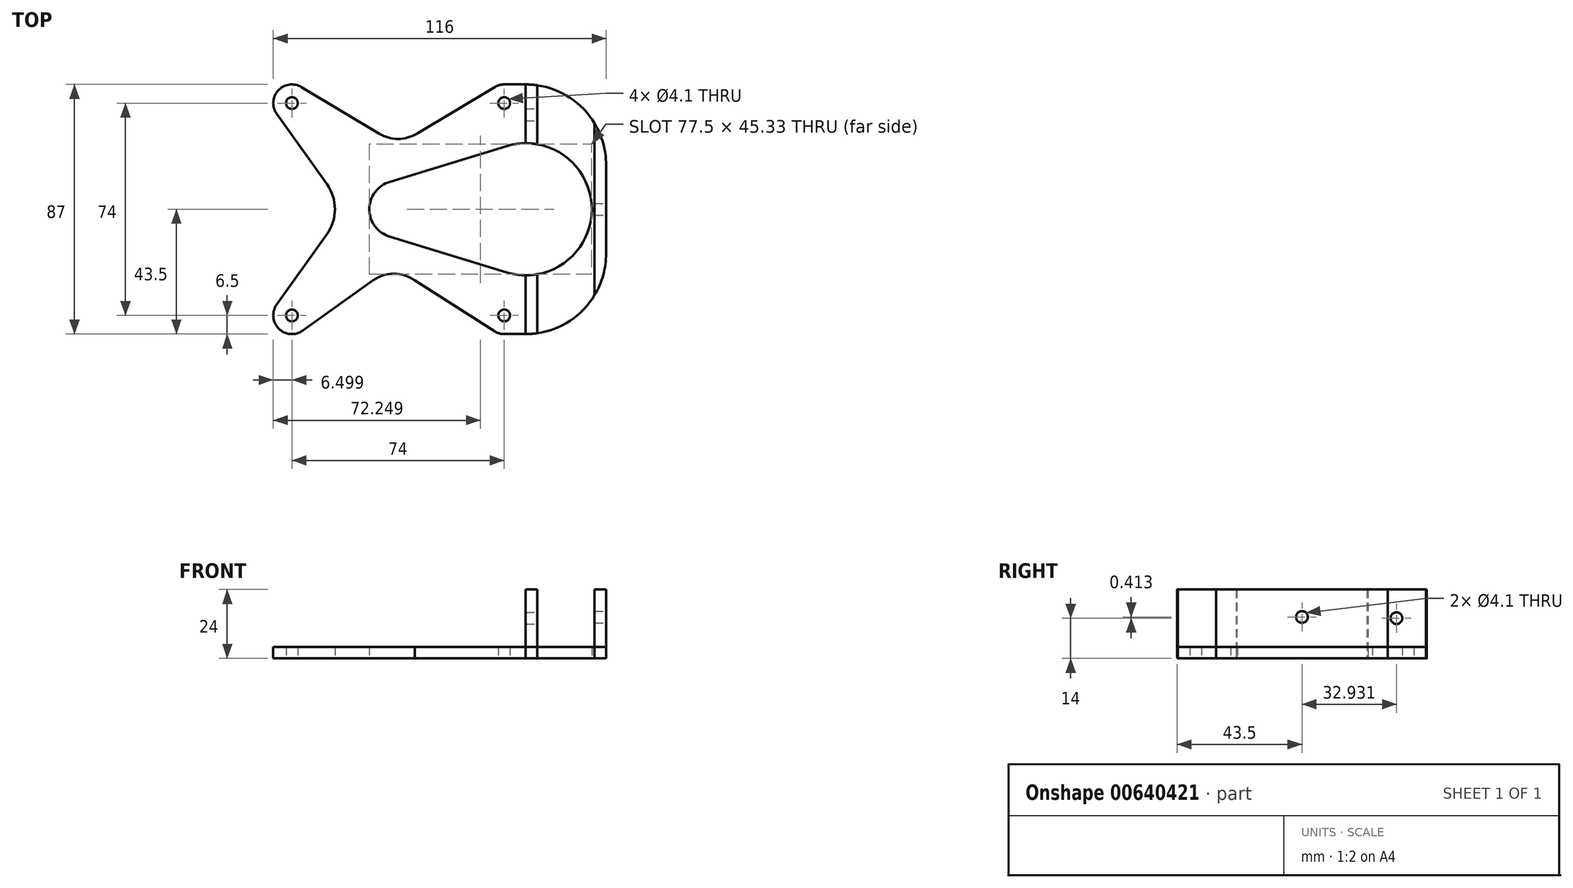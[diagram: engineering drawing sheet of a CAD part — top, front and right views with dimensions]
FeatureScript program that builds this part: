
annotation { "Feature Type Name" : "Feature", "Feature Type Description" : "" }
export const myFeature = defineFeature(function(context is Context, id is Id, definition is map)
    precondition{}
    {
        {
            var Q0;
            Q0=qCreatedBy(makeId("Top.planeOp"),FACE);
            var sketch = newSketch(context, id + "F0", { "sketchPlane" : qUnion([Q0])});
            skLineSegment(sketch, "E0.bottom", {"start": v(-43.02, 41.5) * mm, "end": v(95.48, 41.5) * mm});
            skLineSegment(sketch, "E0.top", {"start": v(-43.02, -41.5) * mm, "end": v(95.48, -41.5) * mm});
            skLineSegment(sketch, "E0.left", {"start": v(-43.02, 41.5) * mm, "end": v(-43.02, -41.5) * mm});
            skLineSegment(sketch, "E0.right", {"start": v(95.48, 41.5) * mm, "end": v(95.48, -41.5) * mm});
            skLineSegment(sketch, "E1", {"start": v(-34.02, 60.46) * mm, "end": v(-34.02, -47.61) * mm, "construction": true});
            skLineSegment(sketch, "E2", {"start": v(-53.58, 0) * mm, "end": v(72.53, 0) * mm, "construction": true});
            skLineSegment(sketch, "E3", {"start": v(-46.55, 37) * mm, "end": v(71.96, 37) * mm, "construction": true});
            skLineSegment(sketch, "E4", {"start": v(-45.6, -37) * mm, "end": v(74.43, -37) * mm, "construction": true});
            skLineSegment(sketch, "E5", {"start": v(39.98, 59.32) * mm, "end": v(39.98, -47.8) * mm, "construction": true});
            skCircle(sketch, "E6", {"center": v(-34.02, 37) * mm, "radius": 2.05 * mm});
            skCircle(sketch, "E7", {"center": v(-34.02, -37) * mm, "radius": 2.05 * mm});
            skCircle(sketch, "E8", {"center": v(39.98, 37) * mm, "radius": 2.05 * mm});
            skCircle(sketch, "E9", {"center": v(39.98, -37) * mm, "radius": 2.05 * mm});
            skLineSegment(sketch, "E10", {"start": v(47.48, 53.05) * mm, "end": v(47.48, -49.7) * mm, "construction": true});
            skLineSegment(sketch, "E11", {"start": v(71.48, 54) * mm, "end": v(71.48, 41.5) * mm, "construction": true});
            skLineSegment(sketch, "E12", {"start": v(51.48, 53.2) * mm, "end": v(51.48, -45.93) * mm, "construction": true});
            skLineSegment(sketch, "E13", {"start": v(75.48, 54.1) * mm, "end": v(75.48, 41.5) * mm, "construction": true});
            skArc(sketch, "E14", {"start": v(-30.68, 42.58) * mm, "mid": v(-38.8, 41.4) * mm, "end": v(-39.31, 33.22) * mm});
            skArc(sketch, "E15", {"start": v(-39.31, -33.22) * mm, "mid": v(-38.62, -41.6) * mm, "end": v(-30.24, -42.29) * mm});
            skArc(sketch, "E16", {"start": v(36.48, -42.48) * mm, "mid": v(38.16, -43.24) * mm, "end": v(39.98, -43.5) * mm});
            skLineSegment(sketch, "E17", {"start": v(2.98, 52.33) * mm, "end": v(2.98, -45.98) * mm, "construction": true});
            skArc(sketch, "E18", {"start": v(-3.44, 26.27) * mm, "mid": v(2.98, 24.5) * mm, "end": v(9.4, 26.27) * mm});
            skArc(sketch, "E19", {"start": v(40.76, -22) * mm, "mid": v(70.48, 0) * mm, "end": v(40.76, 22) * mm});
            skArc(sketch, "E20", {"start": v(0.06, 9.56) * mm, "mid": v(-7.02, 0) * mm, "end": v(0.06, -9.56) * mm});
            skLineSegment(sketch, "E21", {"start": v(-39.31, 33.22) * mm, "end": v(-21.81, 8.72) * mm});
            skLineSegment(sketch, "E22", {"start": v(-30.68, 42.58) * mm, "end": v(-3.44, 26.27) * mm});
            skLineSegment(sketch, "E23", {"start": v(-21.81, -8.72) * mm, "end": v(-39.31, -33.22) * mm});
            skLineSegment(sketch, "E24", {"start": v(-30.24, -42.29) * mm, "end": v(-5.74, -24.8) * mm});
            skLineSegment(sketch, "E25", {"start": v(36.48, -42.48) * mm, "end": v(8.79, -24.8) * mm});
            skLineSegment(sketch, "E26", {"start": v(0.06, 9.56) * mm, "end": v(40.76, 22) * mm});
            skLineSegment(sketch, "E27", {"start": v(0.06, -9.56) * mm, "end": v(40.76, -22) * mm});
            skLineSegment(sketch, "E28", {"start": v(39.98, 43.5) * mm, "end": v(47.48, 43.5) * mm});
            skLineSegment(sketch, "E29", {"start": v(39.98, -43.5) * mm, "end": v(47.48, -43.5) * mm});
            skLineSegment(sketch, "E30", {"start": v(75.48, 43.5) * mm, "end": v(75.48, -43.5) * mm});
            skArc(sketch, "E31.trimOffspring", {"start": v(-21.81, -8.72) * mm, "mid": v(-19.02, 0) * mm, "end": v(-21.81, 8.72) * mm});
            skArc(sketch, "E32.trimOffspring", {"start": v(8.79, -24.8) * mm, "mid": v(1.53, -22.47) * mm, "end": v(-5.74, -24.8) * mm});
            skLineSegment(sketch, "E33", {"start": v(47.48, 43.5) * mm, "end": v(47.48, 23) * mm});
            skLineSegment(sketch, "E34", {"start": v(51.48, 43.5) * mm, "end": v(51.48, 22.65) * mm});
            skLineSegment(sketch, "E35", {"start": v(47.48, -23) * mm, "end": v(47.48, -43.5) * mm});
            skLineSegment(sketch, "E36", {"start": v(51.48, -22.65) * mm, "end": v(51.48, -43.5) * mm});
            skLineSegment(sketch, "E37", {"start": v(71.48, 43.5) * mm, "end": v(71.48, -43.5) * mm});
            skLineSegment(sketch, "E38", {"start": v(102.45, 15.5) * mm, "end": v(-54.14, 15.5) * mm, "construction": true});
            skLineSegment(sketch, "E39", {"start": v(99.99, -15.5) * mm, "end": v(-50.85, -15.5) * mm, "construction": true});
            skArc(sketch, "E40", {"start": v(19.48, 15.5) * mm, "mid": v(19.48, 15.5) * mm, "end": v(19.48, 15.5) * mm});
            skArc(sketch, "E41", {"start": v(47.48, -43.5) * mm, "mid": v(67.28, -35.3) * mm, "end": v(75.48, -15.5) * mm});
            skArc(sketch, "E42.trimOffspring", {"start": v(75.48, 15.5) * mm, "mid": v(67.28, 35.3) * mm, "end": v(47.48, 43.5) * mm});
            skLineSegment(sketch, "E43.trimOffspring", {"start": v(75.48, 15.5) * mm, "end": v(75.48, -45.57) * mm, "construction": true});
            skLineSegment(sketch, "E44.trimOffspring", {"start": v(71.48, 29.92) * mm, "end": v(71.48, -29.92) * mm, "construction": true});
            skArc(sketch, "E45.trimOffspring", {"start": v(19.48, -15.5) * mm, "mid": v(19.48, -15.5) * mm, "end": v(19.48, -15.5) * mm});
            skArc(sketch, "E46", {"start": v(39.98, 43.5) * mm, "mid": v(38.25, 43.27) * mm, "end": v(36.64, 42.58) * mm});
            skLineSegment(sketch, "E47", {"start": v(9.4, 26.27) * mm, "end": v(36.64, 42.58) * mm});
            skLineSegment(sketch, "E48.trimOffspring", {"start": v(71.48, -41.5) * mm, "end": v(71.48, -48) * mm, "construction": true});
            skSolve(sketch);
        }
        {
            var Q0;
            Q0=makeQuery(id+"F0.imprint","IMPRINT",FACE,{"disambiguationData":[TD([[makeQuery(id+"F0.imprint","IMPRINT",EDGE,{"derivedFrom":sQuery(id+"F0.wireOp",EDGE,"E6")}),-1.0]])]});
            var Q1;
            {var subQ0=sQuery(id+"F0.wireOp",EDGE,"E14");var subQ1=sQuery(id+"F0.wireOp",EDGE,"E0.bottom");var subQ2=makeQuery(id+"F0.imprint","INTERSECT",VERTEX,{"derivedFrom":[subQ1,subQ0]});Q1=makeQuery(id+"F0.imprint","IMPRINT",FACE,{"disambiguationData":[TD([[makeQuery(id+"F0.imprint","IMPRINT",EDGE,{"disambiguationData":[TD([[subQ2,-1.0]])],"derivedFrom":subQ1}),1.0]])]});}
            var Q2;
            {var subQ0=sQuery(id+"F0.wireOp",EDGE,"E15");var subQ1=sQuery(id+"F0.wireOp",EDGE,"E0.top");var subQ2=makeQuery(id+"F0.imprint","INTERSECT",VERTEX,{"derivedFrom":[subQ1,subQ0]});Q2=makeQuery(id+"F0.imprint","IMPRINT",FACE,{"disambiguationData":[TD([[makeQuery(id+"F0.imprint","IMPRINT",EDGE,{"disambiguationData":[TD([[subQ2,-1.0]])],"derivedFrom":subQ1}),-1.0]])]});}
            var Q3;
            {var subQ2=sQuery(id+"F0.wireOp",EDGE,"E28");Q3=makeQuery(id+"F0.imprint","IMPRINT",FACE,{"disambiguationData":[TD([[makeQuery(id+"F0.imprint","IMPRINT",EDGE,{"derivedFrom":subQ2}),-1.0]])]});}
            var Q4;
            {var subQ0=sQuery(id+"F0.wireOp",EDGE,"E33");var subQ1=sQuery(id+"F0.wireOp",EDGE,"E0.bottom");var subQ2=makeQuery(id+"F0.imprint","INTERSECT",VERTEX,{"derivedFrom":[subQ1,subQ0]});Q4=makeQuery(id+"F0.imprint","IMPRINT",FACE,{"disambiguationData":[TD([[makeQuery(id+"F0.imprint","IMPRINT",EDGE,{"disambiguationData":[TD([[subQ2,-1.0]])],"derivedFrom":subQ1}),1.0]])]});}
            var Q5;
            {var subQ0=sQuery(id+"F0.wireOp",EDGE,"E33");var subQ1=sQuery(id+"F0.wireOp",EDGE,"E0.bottom");var subQ2=makeQuery(id+"F0.imprint","INTERSECT",VERTEX,{"derivedFrom":[subQ1,subQ0]});Q5=makeQuery(id+"F0.imprint","IMPRINT",FACE,{"disambiguationData":[TD([[makeQuery(id+"F0.imprint","IMPRINT",EDGE,{"disambiguationData":[TD([[subQ2,-1.0]])],"derivedFrom":subQ1}),-1.0]])]});}
            var Q6;
            {var subQ3=sQuery(id+"F0.wireOp",EDGE,"E0.bottom");var subQ11=sQuery(id+"F0.wireOp",EDGE,"E42.trimOffspring");var subQ12=makeQuery(id+"F0.imprint","INTERSECT",VERTEX,{"derivedFrom":[subQ3,subQ11]});Q6=makeQuery(id+"F0.imprint","IMPRINT",FACE,{"disambiguationData":[TD([[makeQuery(id+"F0.imprint","IMPRINT",EDGE,{"disambiguationData":[TD([[subQ12,1.0]])],"derivedFrom":subQ3}),-1.0]])]});}
            var Q7;
            {var subQ0=sQuery(id+"F0.wireOp",EDGE,"E42.trimOffspring");var subQ1=sQuery(id+"F0.wireOp",EDGE,"E0.bottom");var subQ2=makeQuery(id+"F0.imprint","INTERSECT",VERTEX,{"derivedFrom":[subQ1,subQ0]});Q7=makeQuery(id+"F0.imprint","IMPRINT",FACE,{"disambiguationData":[TD([[makeQuery(id+"F0.imprint","IMPRINT",EDGE,{"disambiguationData":[TD([[subQ2,1.0]])],"derivedFrom":subQ1}),1.0]])]});}
            var Q8;
            {var subQ0=sQuery(id+"F0.wireOp",EDGE,"E41");var subQ1=sQuery(id+"F0.wireOp",EDGE,"E30");var subQ2=makeQuery(id+"F0.imprint","INTERSECT",VERTEX,{"derivedFrom":[subQ1,subQ0]});Q8=makeQuery(id+"F0.imprint","IMPRINT",FACE,{"disambiguationData":[TD([[makeQuery(id+"F0.imprint","IMPRINT",EDGE,{"disambiguationData":[TD([[subQ2,1.0]])],"derivedFrom":subQ1}),-1.0]])]});}
            var Q9;
            {var subQ0=sQuery(id+"F0.wireOp",EDGE,"E35");var subQ1=sQuery(id+"F0.wireOp",EDGE,"E0.top");var subQ2=makeQuery(id+"F0.imprint","INTERSECT",VERTEX,{"derivedFrom":[subQ1,subQ0]});Q9=makeQuery(id+"F0.imprint","IMPRINT",FACE,{"disambiguationData":[TD([[makeQuery(id+"F0.imprint","IMPRINT",EDGE,{"disambiguationData":[TD([[subQ2,-1.0]])],"derivedFrom":subQ1}),1.0]])]});}
            var Q10;
            {var subQ0=sQuery(id+"F0.wireOp",EDGE,"E41");var subQ1=sQuery(id+"F0.wireOp",EDGE,"E0.top");var subQ2=makeQuery(id+"F0.imprint","INTERSECT",VERTEX,{"derivedFrom":[subQ1,subQ0]});Q10=makeQuery(id+"F0.imprint","IMPRINT",FACE,{"disambiguationData":[TD([[makeQuery(id+"F0.imprint","IMPRINT",EDGE,{"disambiguationData":[TD([[subQ2,1.0]])],"derivedFrom":subQ1}),-1.0]])]});}
            var Q11;
            {var subQ0=sQuery(id+"F0.wireOp",EDGE,"E35");var subQ1=sQuery(id+"F0.wireOp",EDGE,"E0.top");var subQ2=makeQuery(id+"F0.imprint","INTERSECT",VERTEX,{"derivedFrom":[subQ1,subQ0]});Q11=makeQuery(id+"F0.imprint","IMPRINT",FACE,{"disambiguationData":[TD([[makeQuery(id+"F0.imprint","IMPRINT",EDGE,{"disambiguationData":[TD([[subQ2,-1.0]])],"derivedFrom":subQ1}),-1.0]])]});}
            var Q12;
            {var subQ4=sQuery(id+"F0.wireOp",EDGE,"E16");Q12=makeQuery(id+"F0.imprint","IMPRINT",FACE,{"disambiguationData":[TD([[makeQuery(id+"F0.imprint","IMPRINT",EDGE,{"derivedFrom":subQ4}),1.0]])]});}
            extrude(context, id + "F1", {"entities" : qUnion([Q0, Q1, Q2, Q3, Q4, Q5, Q6, Q7, Q8, Q9, Q10, Q11, Q12]), "depth" : 4 * mm, "offsetDistance" : 25 * mm});
        }
        {
            var Q0;
            {var subQ0=sQuery(id+"F0.wireOp",EDGE,"E33");var subQ1=sQuery(id+"F0.wireOp",EDGE,"E0.bottom");var subQ2=makeQuery(id+"F0.imprint","INTERSECT",VERTEX,{"derivedFrom":[subQ1,subQ0]});Q0=makeQuery(id+"F0.imprint","IMPRINT",FACE,{"disambiguationData":[TD([[makeQuery(id+"F0.imprint","IMPRINT",EDGE,{"disambiguationData":[TD([[subQ2,-1.0]])],"derivedFrom":subQ1}),1.0]])]});}
            var Q1;
            {var subQ0=sQuery(id+"F0.wireOp",EDGE,"E33");var subQ1=sQuery(id+"F0.wireOp",EDGE,"E0.bottom");var subQ2=makeQuery(id+"F0.imprint","INTERSECT",VERTEX,{"derivedFrom":[subQ1,subQ0]});Q1=makeQuery(id+"F0.imprint","IMPRINT",FACE,{"disambiguationData":[TD([[makeQuery(id+"F0.imprint","IMPRINT",EDGE,{"disambiguationData":[TD([[subQ2,-1.0]])],"derivedFrom":subQ1}),-1.0]])]});}
            var Q2;
            {var subQ0=sQuery(id+"F0.wireOp",EDGE,"E41");var subQ1=sQuery(id+"F0.wireOp",EDGE,"E30");var subQ2=makeQuery(id+"F0.imprint","INTERSECT",VERTEX,{"derivedFrom":[subQ1,subQ0]});Q2=makeQuery(id+"F0.imprint","IMPRINT",FACE,{"disambiguationData":[TD([[makeQuery(id+"F0.imprint","IMPRINT",EDGE,{"disambiguationData":[TD([[subQ2,1.0]])],"derivedFrom":subQ1}),-1.0]])]});}
            var Q3;
            {var subQ0=sQuery(id+"F0.wireOp",EDGE,"E35");var subQ1=sQuery(id+"F0.wireOp",EDGE,"E0.top");var subQ2=makeQuery(id+"F0.imprint","INTERSECT",VERTEX,{"derivedFrom":[subQ1,subQ0]});Q3=makeQuery(id+"F0.imprint","IMPRINT",FACE,{"disambiguationData":[TD([[makeQuery(id+"F0.imprint","IMPRINT",EDGE,{"disambiguationData":[TD([[subQ2,-1.0]])],"derivedFrom":subQ1}),1.0]])]});}
            var Q4;
            {var subQ0=sQuery(id+"F0.wireOp",EDGE,"E35");var subQ1=sQuery(id+"F0.wireOp",EDGE,"E0.top");var subQ2=makeQuery(id+"F0.imprint","INTERSECT",VERTEX,{"derivedFrom":[subQ1,subQ0]});Q4=makeQuery(id+"F0.imprint","IMPRINT",FACE,{"disambiguationData":[TD([[makeQuery(id+"F0.imprint","IMPRINT",EDGE,{"disambiguationData":[TD([[subQ2,-1.0]])],"derivedFrom":subQ1}),-1.0]])]});}
            extrude(context, id + "F2", {"entities" : qUnion([Q0, Q1, Q2, Q3, Q4]), "depth" : 24 * mm, "offsetDistance" : 25 * mm});
        }
        {
            var Q0;
            Q0=makeQuery(id+"F2.opExtrude","SWEPT_FACE",FACE,{"disambiguationData":[OSD([sQuery(id+"F0.wireOp",EDGE,"E34")])]});
            var sketch = newSketch(context, id + "F3", { "sketchPlane" : qUnion([Q0])});
            skPoint(sketch, "E49", {"position": v(32.93, 24) * mm});
            skLineSegment(sketch, "E50", {"start": v(32.93, 24) * mm, "end": v(32.93, 9.03) * mm, "construction": true});
            skCircle(sketch, "E51", {"center": v(32.93, 14) * mm, "radius": 2.05 * mm});
            skCircle(sketch, "E52.MirrorC", {"center": v(-32.93, 14) * mm, "radius": 2.05 * mm});
            skSolve(sketch);
        }
        {
            var Q0;
            Q0=makeQuery(id+"F3.imprint","IMPRINT",FACE,{"disambiguationData":[TD([[makeQuery(id+"F3.imprint","IMPRINT",EDGE,{"derivedFrom":sQuery(id+"F3.wireOp",EDGE,"E52.MirrorC")}),-1.0]])]});
            var Q1;
            Q1=makeQuery(id+"F3.imprint","IMPRINT",FACE,{"disambiguationData":[TD([[makeQuery(id+"F3.imprint","IMPRINT",EDGE,{"derivedFrom":sQuery(id+"F3.wireOp",EDGE,"E51")}),1.0]])]});
            extrude(context, id + "F4", {"entities" : qUnion([Q0, Q1]), "operationType" : NewBodyOperationType.REMOVE, "endBound" : BoundingType.SYMMETRIC, "oppositeDirection" : true, "depth" : 8 * mm, "offsetDistance" : 25 * mm});
        }
        {
            var Q0;
            Q0=makeQuery(id+"F2.opExtrude","SWEPT_FACE",FACE,{"disambiguationData":[OSD([sQuery(id+"F0.wireOp",EDGE,"E30")])]});
            var sketch = newSketch(context, id + "F5", { "sketchPlane" : qUnion([Q0])});
            skCircle(sketch, "E53", {"center": v(0, 14.41) * mm, "radius": 2.05 * mm});
            skPoint(sketch, "E53.centerSnap0", {"position": v(0, 24) * mm});
            skSolve(sketch);
        }
        {
            var Q0;
            Q0=makeQuery(id+"F5.imprint","IMPRINT",FACE,{"disambiguationData":[TD([[makeQuery(id+"F5.imprint","IMPRINT",EDGE,{"derivedFrom":sQuery(id+"F5.wireOp",EDGE,"E53")}),1.0]])]});
            extrude(context, id + "F6", {"entities" : qUnion([Q0]), "operationType" : NewBodyOperationType.REMOVE, "oppositeDirection" : true, "depth" : 8 * mm, "offsetDistance" : 25 * mm});
        }
    });
